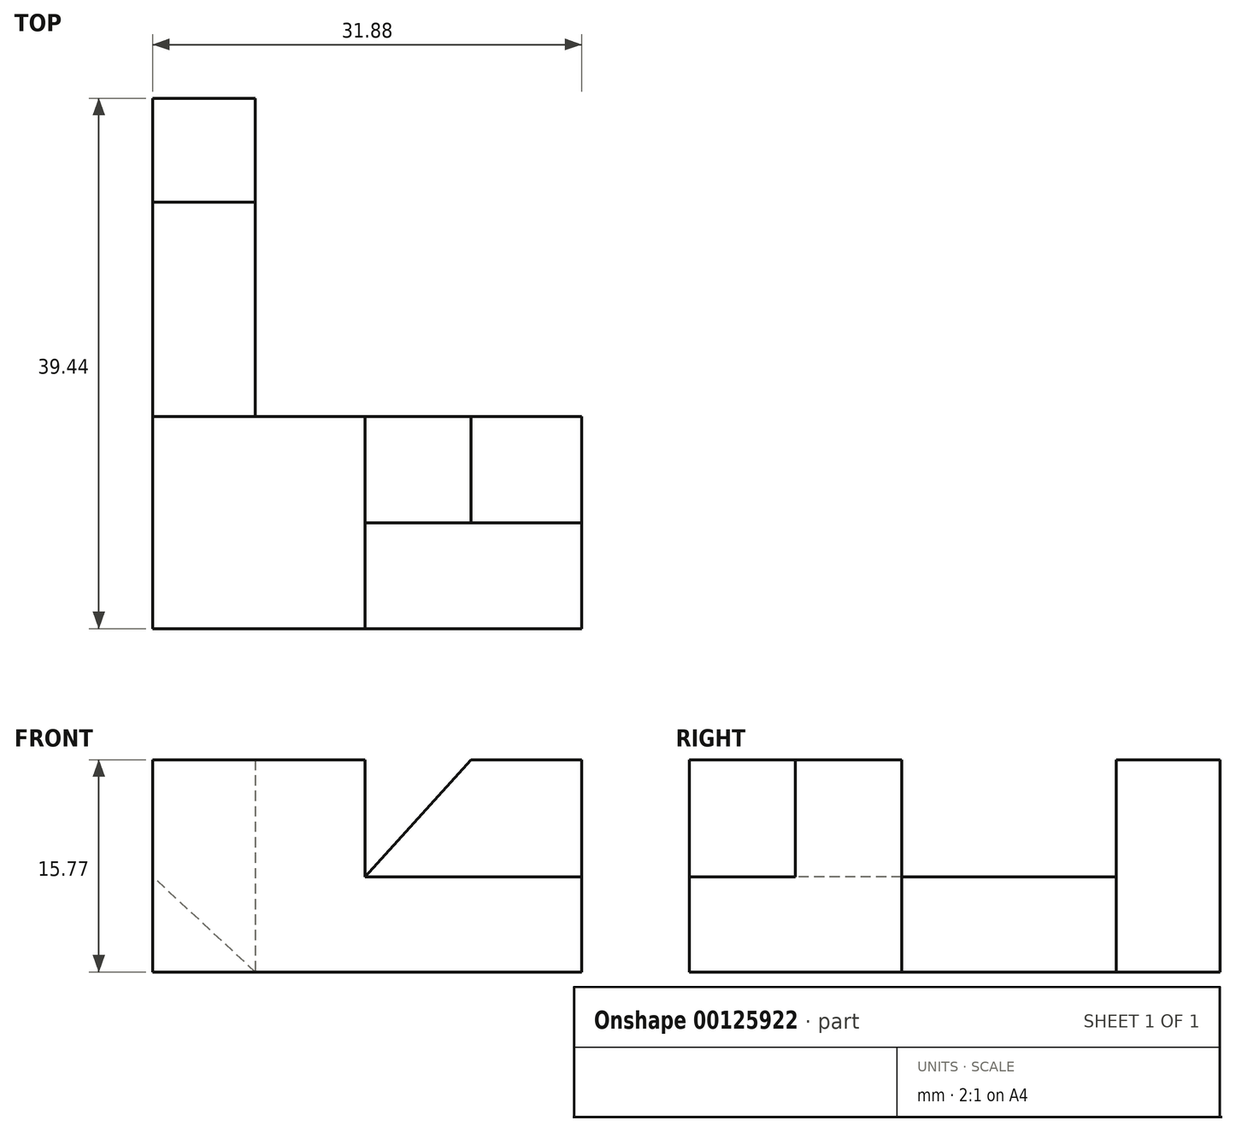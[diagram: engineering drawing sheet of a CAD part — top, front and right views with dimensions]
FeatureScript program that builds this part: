
annotation { "Feature Type Name" : "Feature", "Feature Type Description" : "" }
export const myFeature = defineFeature(function(context is Context, id is Id, definition is map)
    precondition{}
    {
        {
            var Q0;
            Q0=qCreatedBy(makeId("Front.planeOp"),FACE);
            var sketch = newSketch(context, id + "F0", { "sketchPlane" : qUnion([Q0])});
            skLineSegment(sketch, "E0", {"start": v(-7.37, 3.48) * mm, "end": v(-7.37, -12.3) * mm});
            skLineSegment(sketch, "E1", {"start": v(-7.37, -12.3) * mm, "end": v(8.4, -12.3) * mm});
            skLineSegment(sketch, "E2", {"start": v(8.4, -12.3) * mm, "end": v(8.4, 3.48) * mm});
            skLineSegment(sketch, "E3", {"start": v(8.4, 3.48) * mm, "end": v(-7.37, 3.48) * mm});
            skSolve(sketch);
        }
        {
            var Q0;
            Q0=makeQuery(id+"F0.imprint","IMPRINT",FACE,{"disambiguationData":[TD([[makeQuery(id+"F0.imprint","IMPRINT",EDGE,{"derivedFrom":sQuery(id+"F0.wireOp",EDGE,"E0")}),1.0]])]});
            extrude(context, id + "F1", {"entities" : qUnion([Q0]), "depth" : 15.77 * mm});
        }
        {
            var Q0;
            Q0=makeQuery(id+"F1.opExtrude","CAP_FACE",FACE,{"disambiguationData":[OSD([sQuery(id+"F0.wireOp",EDGE,"E0"),sQuery(id+"F0.wireOp",EDGE,"E1"),sQuery(id+"F0.wireOp",EDGE,"E2"),sQuery(id+"F0.wireOp",EDGE,"E3")])],"isStart":true});
            var sketch = newSketch(context, id + "F2", { "sketchPlane" : qUnion([Q0])});
            skLineSegment(sketch, "E4", {"start": v(7.37, -5.2) * mm, "end": v(7.37, -12.3) * mm});
            skLineSegment(sketch, "E5", {"start": v(7.37, -12.3) * mm, "end": v(-0.25, -12.3) * mm});
            skLineSegment(sketch, "E6", {"start": v(-0.25, -12.3) * mm, "end": v(7.37, -5.2) * mm});
            skSolve(sketch);
        }
        {
            var Q0;
            Q0=qSketchRegion(id+"F2",true);
            extrude(context, id + "F3", {"entities" : qUnion([Q0]), "operationType" : NewBodyOperationType.ADD, "depth" : 15.95 * mm});
        }
        {
            var Q0;
            Q0=makeQuery(id+"F3.opExtrude","CAP_FACE",FACE,{"disambiguationData":[OSD([sQuery(id+"F2.wireOp",EDGE,"E4"),sQuery(id+"F2.wireOp",EDGE,"E5"),sQuery(id+"F2.wireOp",EDGE,"E6")])],"isStart":false});
            var sketch = newSketch(context, id + "F4", { "sketchPlane" : qUnion([Q0])});
            skLineSegment(sketch, "E7.0.0", {"start": v(-8.4, -12.3) * mm, "end": v(-0.25, -12.3) * mm});
            skLineSegment(sketch, "E7.0.1", {"start": v(-0.25, -12.3) * mm, "end": v(7.37, -5.2) * mm});
            skLineSegment(sketch, "E7.0.2", {"start": v(7.37, -5.2) * mm, "end": v(7.37, 3.48) * mm});
            skLineSegment(sketch, "E7.0.3", {"start": v(7.37, 3.48) * mm, "end": v(-8.4, 3.48) * mm});
            skLineSegment(sketch, "E7.0.4", {"start": v(-8.4, 3.48) * mm, "end": v(-8.4, -12.3) * mm});
            skLineSegment(sketch, "E8", {"start": v(7.37, -12.3) * mm, "end": v(7.37, 3.48) * mm});
            skLineSegment(sketch, "E9", {"start": v(-0.25, 3.48) * mm, "end": v(7.37, 3.48) * mm});
            skPoint(sketch, "E9.startSnap0", {"position": v(-0.52, 3.48) * mm});
            skLineSegment(sketch, "E10", {"start": v(-0.25, 3.48) * mm, "end": v(-0.25, -12.3) * mm});
            skLineSegment(sketch, "E11", {"start": v(-0.25, -12.3) * mm, "end": v(7.37, -12.3) * mm});
            skSolve(sketch);
        }
        {
            var Q0;
            {var subQ0=sQuery(id+"F4.wireOp",EDGE,"E7.0.1");Q0=makeQuery(id+"F4.imprint","IMPRINT",FACE,{"disambiguationData":[TD([[makeQuery(id+"F4.imprint","IMPRINT",EDGE,{"derivedFrom":subQ0}),-1.0]])]});}
            var Q1;
            {var subQ0=sQuery(id+"F4.wireOp",EDGE,"E7.0.1");Q1=makeQuery(id+"F4.imprint","IMPRINT",FACE,{"disambiguationData":[TD([[makeQuery(id+"F4.imprint","IMPRINT",EDGE,{"derivedFrom":subQ0}),1.0]])]});}
            extrude(context, id + "F5", {"entities" : qUnion([Q0, Q1]), "operationType" : NewBodyOperationType.ADD, "depth" : 7.72 * mm});
        }
        {
            var Q0;
            Q0=makeQuery(id+"F1.opExtrude","SWEPT_FACE",FACE,{"disambiguationData":[OSD([sQuery(id+"F0.wireOp",EDGE,"E2")])]});
            var sketch = newSketch(context, id + "F6", { "sketchPlane" : qUnion([Q0])});
            skLineSegment(sketch, "E12", {"start": v(-15.77, -12.3) * mm, "end": v(-15.77, -5.23) * mm});
            skLineSegment(sketch, "E13", {"start": v(-15.77, -5.23) * mm, "end": v(0, -5.23) * mm});
            skLineSegment(sketch, "E14", {"start": v(0, -5.23) * mm, "end": v(0, -12.3) * mm});
            skLineSegment(sketch, "E15", {"start": v(0, -12.3) * mm, "end": v(-15.77, -12.3) * mm});
            skSolve(sketch);
        }
        {
            var Q0;
            Q0=makeQuery(id+"F6.imprint","IMPRINT",FACE,{"disambiguationData":[TD([[makeQuery(id+"F6.imprint","IMPRINT",EDGE,{"derivedFrom":sQuery(id+"F6.wireOp",EDGE,"E12")}),-1.0]])]});
            extrude(context, id + "F7", {"entities" : qUnion([Q0]), "operationType" : NewBodyOperationType.ADD, "depth" : 16.1 * mm});
        }
        {
            var Q0;
            Q0=makeQuery(id+"F1.opExtrude","SWEPT_FACE",FACE,{"disambiguationData":[OSD([sQuery(id+"F0.wireOp",EDGE,"E2")])]});
            var sketch = newSketch(context, id + "F8", { "sketchPlane" : qUnion([Q0])});
            skLineSegment(sketch, "E16", {"start": v(0, -5.23) * mm, "end": v(0, 3.48) * mm});
            skLineSegment(sketch, "E17", {"start": v(0, 3.48) * mm, "end": v(-7.89, 3.48) * mm});
            skLineSegment(sketch, "E18", {"start": v(-7.89, 3.48) * mm, "end": v(-7.89, -5.23) * mm});
            skLineSegment(sketch, "E19", {"start": v(-7.89, -5.23) * mm, "end": v(0, -5.23) * mm});
            skSolve(sketch);
        }
        {
            var Q0;
            Q0=qSketchRegion(id+"F8",true);
            var Q1;
            Q1=makeQuery(id+"F7.opExtrude","CAP_FACE",FACE,{"disambiguationData":[OSD([sQuery(id+"F6.wireOp",EDGE,"E12"),sQuery(id+"F6.wireOp",EDGE,"E13"),sQuery(id+"F6.wireOp",EDGE,"E14"),sQuery(id+"F6.wireOp",EDGE,"E15")])],"isStart":false});
            extrude(context, id + "F9", {"entities" : qUnion([Q0]), "operationType" : NewBodyOperationType.ADD, "endBound" : BoundingType.UP_TO_SURFACE, "endBoundEntityFace" : qUnion([Q1]), "depth" : 25.4 * mm});
        }
        {
            var Q0;
            Q0=makeQuery(id+"F9.opExtrude","SWEPT_FACE",FACE,{"disambiguationData":[OSD([sQuery(id+"F8.wireOp",EDGE,"E18")])]});
            var sketch = newSketch(context, id + "F10", { "sketchPlane" : qUnion([Q0])});
            skLineSegment(sketch, "E20.0", {"start": v(8.4, 3.48) * mm, "end": v(8.4, -5.23) * mm});
            skLineSegment(sketch, "E21", {"start": v(8.4, 3.48) * mm, "end": v(16.28, 3.48) * mm});
            skLineSegment(sketch, "E22", {"start": v(16.28, 3.48) * mm, "end": v(8.4, -5.23) * mm});
            skSolve(sketch);
        }
        {
            var Q0;
            Q0=qSketchRegion(id+"F10",true);
            extrude(context, id + "F11", {"entities" : qUnion([Q0]), "operationType" : NewBodyOperationType.REMOVE, "oppositeDirection" : true, "depth" : 25.4 * mm});
        }
    });
